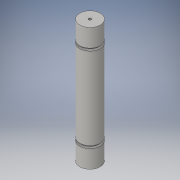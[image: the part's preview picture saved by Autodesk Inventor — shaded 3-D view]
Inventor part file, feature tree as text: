
AUTODESK INVENTOR PART (.ipt)
format: ipt  version: 2016 (Build 200138000, 138)  size: 117,760 bytes
history: native  units: in
note: dims shown in document units (in); Inventor stores cm internally (conversion verified against a paired STEP export)
features: sketch x2, revolve x1, hole x1
ambient origin geometry x8: Origin, YZ Plane, XZ Plane, XY Plane, X Axis, Y Axis, Z Axis, Center Point
bodies: Solid1 (feature_tree)
feature tree (4):
  revolve  "Revolution1"  [1 undecoded]
  hole  "Hole1"  [1 undecoded]
  sketch  "Sketch1"  dims[d2=90.0deg d3=0.25in]
  sketch  "Sketch2"  dims[d4=0.25in d5=0.25in d7=0.25in d8=1.0in d9=1.0in d10=1.0in d11=12.0in d12=6.0in d13=4.0in d14=4.0in d15=0.26in d16=0.75in d17=0.375in d18=0.25in d19=0.5635in d20=1.0in d21=0.8108in]
note: 2 required parameter values undecoded (feature->parameter linkage not recoverable at this tier; creation-order binding heuristic only, values carry confidence <= 0.55)